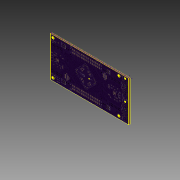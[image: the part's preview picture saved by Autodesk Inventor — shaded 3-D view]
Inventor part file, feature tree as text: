
AUTODESK INVENTOR PART (.ipt)
format: ipt  version: 2015 (Build 190159000, 159)  size: 1,391,104 bytes
history: native  units: in
note: dims shown in document units (in); Inventor stores cm internally (conversion verified against a paired STEP export)
features: sketch x4, extrude x2, other x2, projected_geometry x2
ambient origin geometry x8: Origin, YZ Plane, XZ Plane, XY Plane, X Axis, Y Axis, Z Axis, Center Point
bodies: Solid1 (feature_tree)
feature tree (10):
  extrude  "Extrusion1"  Depth=4.4in
  extrude  "Extrusion3"  Depth=2.25in
  sketch  "Sketch4"  dims[d6=0.1102in]
  sketch  "Sketch5"  dims[d8=0.1102in d10=1.95in d15=0.0787in d16=0.1969in d17=0.1969in d18=0.0394in d19=0.1181in d20=0.0in d21=0.15in d22=0.15in d23=0.15in d28=0.15in d30=2.5in d33=1.3469in d34=1.3469in d35=0.078in d36=0.2in d37=0.1067in d38=0.1102in d39=0.15in d40=0.55in d41=2.5in d42=0.063in d43=0.2in d44=0.1067in]
  sketch  "Sketch1"  dims[d0=0.0646in d1=0.0in d2=4.4in]
  sketch  "Sketch3"  dims[d4=2.25in d5=1.95in]
  other  "Image1"
  projected_geometry  "Projected Loop1"
  projected_geometry  "Projected Loop2"
  other  "Image3"
